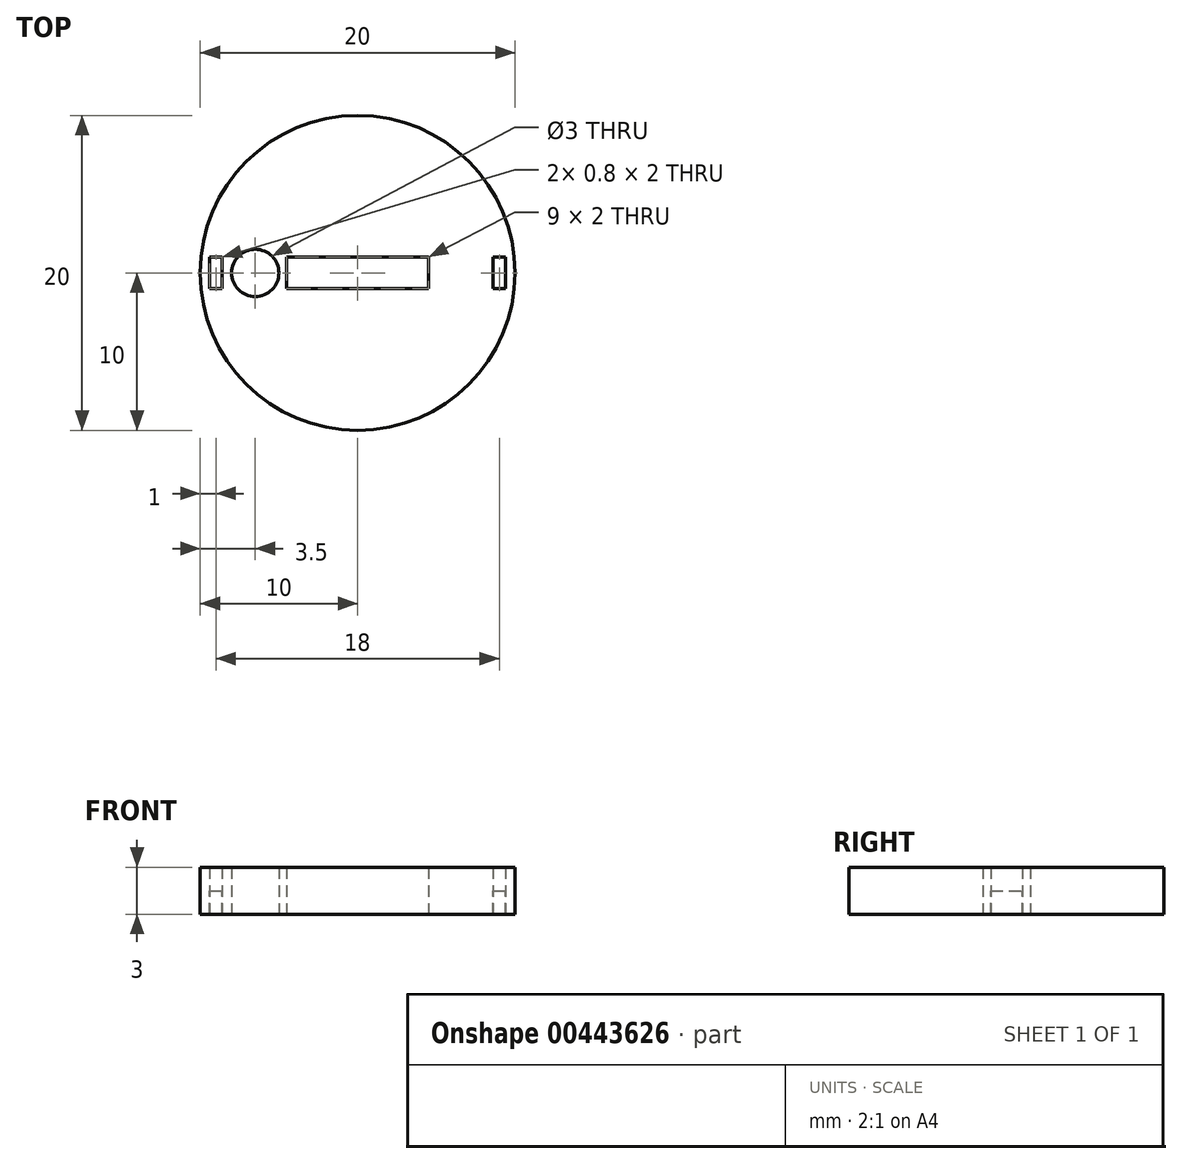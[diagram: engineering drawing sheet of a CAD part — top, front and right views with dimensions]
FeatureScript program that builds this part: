
annotation { "Feature Type Name" : "Feature", "Feature Type Description" : "" }
export const myFeature = defineFeature(function(context is Context, id is Id, definition is map)
    precondition{}
    {
        {
            var Q0;
            Q0=qCreatedBy(makeId("Top.planeOp"),FACE);
            var sketch = newSketch(context, id + "F0", { "sketchPlane" : qUnion([Q0])});
            skCircle(sketch, "E0", {"center": v(0, 0) * mm, "radius": 10 * mm});
            skCircle(sketch, "E1", {"center": v(-6.5, 0) * mm, "radius": 1.5 * mm});
            skLineSegment(sketch, "E2.bottom", {"start": v(-9.4, -1) * mm, "end": v(-8.6, -1) * mm});
            skLineSegment(sketch, "E2.top", {"start": v(-9.4, 1) * mm, "end": v(-8.6, 1) * mm});
            skLineSegment(sketch, "E2.left", {"start": v(-9.4, -1) * mm, "end": v(-9.4, 1) * mm});
            skLineSegment(sketch, "E2.right", {"start": v(-8.6, -1) * mm, "end": v(-8.6, 1) * mm});
            skLineSegment(sketch, "E3.bottom", {"start": v(8.6, -1) * mm, "end": v(9.4, -1) * mm});
            skLineSegment(sketch, "E3.top", {"start": v(8.6, 1) * mm, "end": v(9.4, 1) * mm});
            skLineSegment(sketch, "E3.left", {"start": v(8.6, -1) * mm, "end": v(8.6, 1) * mm});
            skLineSegment(sketch, "E3.right", {"start": v(9.4, -1) * mm, "end": v(9.4, 1) * mm});
            skLineSegment(sketch, "E4.bottom", {"start": v(-4.5, 1) * mm, "end": v(4.5, 1) * mm});
            skLineSegment(sketch, "E4.top", {"start": v(-4.5, -1) * mm, "end": v(4.5, -1) * mm});
            skLineSegment(sketch, "E4.left", {"start": v(-4.5, 1) * mm, "end": v(-4.5, -1) * mm});
            skLineSegment(sketch, "E4.right", {"start": v(4.5, 1) * mm, "end": v(4.5, -1) * mm});
            skSolve(sketch);
        }
        {
            var Q0;
            Q0=makeQuery(id+"F0.imprint","IMPRINT",FACE,{"disambiguationData":[TD([[makeQuery(id+"F0.imprint","IMPRINT",EDGE,{"derivedFrom":sQuery(id+"F0.wireOp",EDGE,"E2.bottom")}),1.0]])]});
            var Q1;
            Q1=makeQuery(id+"F0.imprint","IMPRINT",FACE,{"disambiguationData":[TD([[makeQuery(id+"F0.imprint","IMPRINT",EDGE,{"derivedFrom":sQuery(id+"F0.wireOp",EDGE,"E3.bottom")}),1.0]])]});
            extrude(context, id + "F1", {"entities" : qUnion([Q0, Q1]), "depth" : 0 * mm, "hasSecondDirection" : true, "secondDirectionOppositeDirection" : true, "secondDirectionDepth" : 1.5 * mm});
        }
        {
            var Q0;
            Q0 = qSketchRegion(id + "F0", true);
            extrude(context, id + "F2", {"entities" : qUnion([Q0]), "depth" : 1.5 * mm, "hasSecondDirection" : true, "secondDirectionOppositeDirection" : true, "secondDirectionDepth" : 1.5 * mm});
        }
    });
